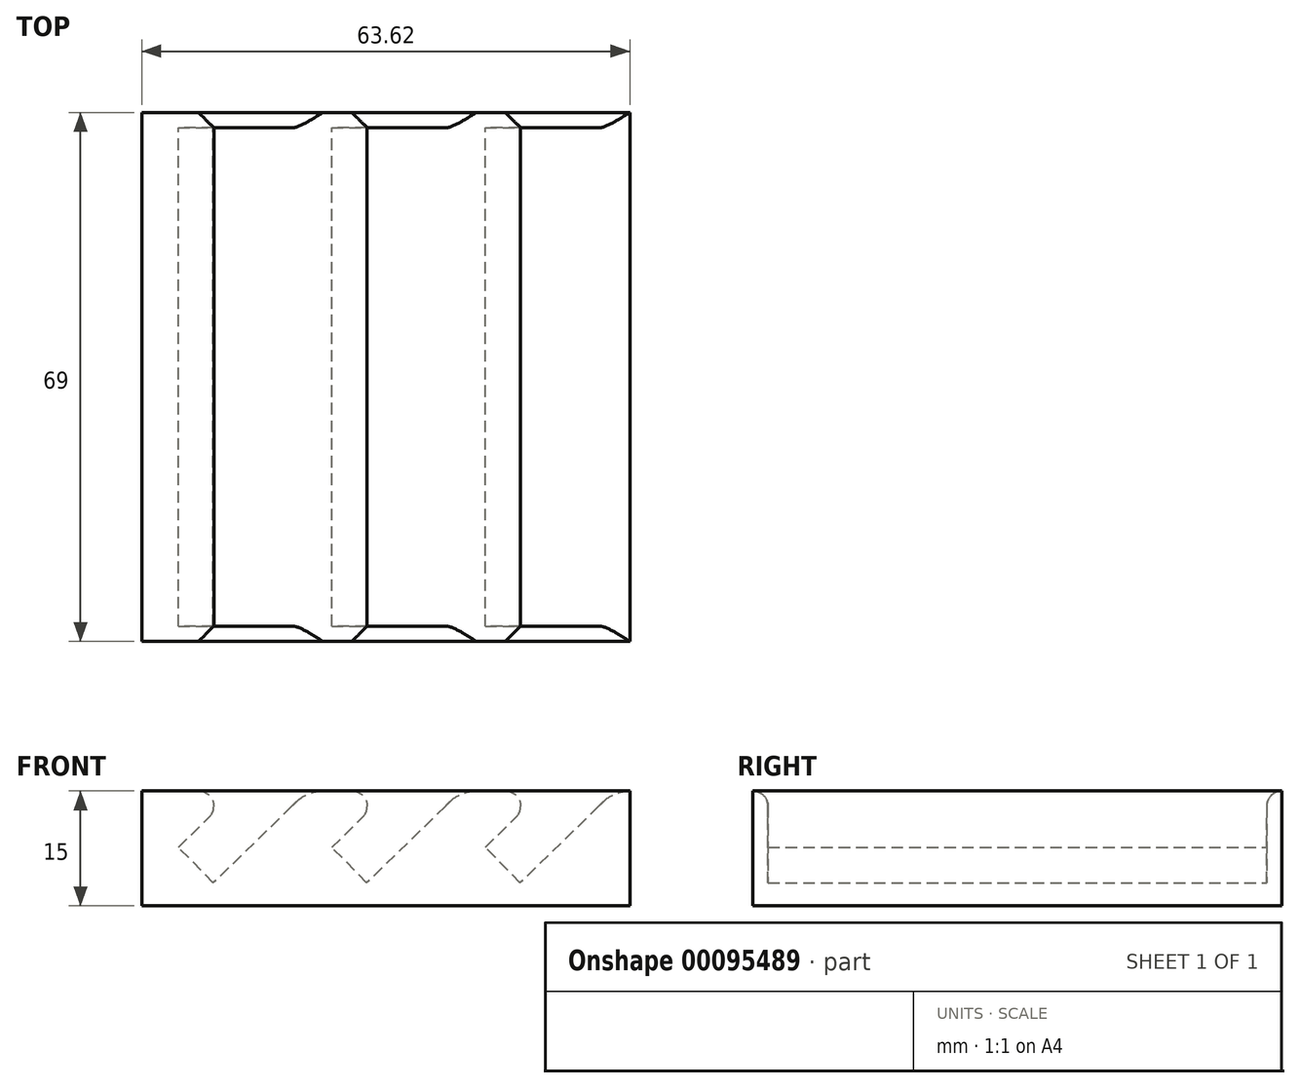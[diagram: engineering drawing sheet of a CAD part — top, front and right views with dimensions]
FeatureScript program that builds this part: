
annotation { "Feature Type Name" : "Feature", "Feature Type Description" : "" }
export const myFeature = defineFeature(function(context is Context, id is Id, definition is map)
    precondition{}
    {
        {
            var Q0;
            Q0=qCreatedBy(makeId("Front.planeOp"),FACE);
            var sketch = newSketch(context, id + "F0", { "sketchPlane" : qUnion([Q0])});
            skLineSegment(sketch, "E0.bottom", {"start": v(0, 0) * mm, "end": v(85.92, 0) * mm});
            skLineSegment(sketch, "E0.top", {"start": v(68.62, 15) * mm, "end": v(85.92, 15) * mm});
            skLineSegment(sketch, "E0.left", {"start": v(0, 0) * mm, "end": v(0, 15) * mm});
            skLineSegment(sketch, "E0.right", {"start": v(85.92, 0) * mm, "end": v(85.92, 15) * mm});
            skLineSegment(sketch, "E1", {"start": v(0, 3) * mm, "end": v(5, 3) * mm});
            skLineSegment(sketch, "E2", {"start": v(5, 3) * mm, "end": v(71.51, 68) * mm, "construction": true});
            skLineSegment(sketch, "E3", {"start": v(5, 3) * mm, "end": v(17.28, 15) * mm});
            skLineSegment(sketch, "E4", {"start": v(5, 3) * mm, "end": v(5.22, 3) * mm});
            skLineSegment(sketch, "E5", {"start": v(5.22, 3) * mm, "end": v(85.92, 3) * mm});
            skLineSegment(sketch, "E6", {"start": v(71.51, 68) * mm, "end": v(76.06, 63.35) * mm, "construction": true});
            skLineSegment(sketch, "E7", {"start": v(76.06, 63.35) * mm, "end": v(14.3, 3) * mm, "construction": true});
            skLineSegment(sketch, "E8", {"start": v(25.12, 13.58) * mm, "end": v(14.3, 3) * mm});
            skLineSegment(sketch, "E9.1.0.0", {"start": v(25, 3) * mm, "end": v(37.28, 15) * mm});
            skLineSegment(sketch, "E9.1.0.3", {"start": v(96.06, 63.35) * mm, "end": v(34.3, 3) * mm, "construction": true});
            skLineSegment(sketch, "E9.1.0.4", {"start": v(25, 3) * mm, "end": v(91.51, 68) * mm, "construction": true});
            skLineSegment(sketch, "E9.1.0.5", {"start": v(91.51, 68) * mm, "end": v(96.06, 63.35) * mm, "construction": true});
            skLineSegment(sketch, "E9.2.0.0", {"start": v(45, 3) * mm, "end": v(57.28, 15) * mm});
            skLineSegment(sketch, "E9.2.0.2", {"start": v(65.12, 13.58) * mm, "end": v(54.3, 3) * mm});
            skLineSegment(sketch, "E9.2.0.3", {"start": v(116.06, 63.35) * mm, "end": v(54.3, 3) * mm, "construction": true});
            skLineSegment(sketch, "E9.2.0.4", {"start": v(45, 3) * mm, "end": v(111.51, 68) * mm, "construction": true});
            skLineSegment(sketch, "E9.2.0.5", {"start": v(111.51, 68) * mm, "end": v(116.06, 63.35) * mm, "construction": true});
            skLineSegment(sketch, "E9.direction1", {"start": v(5, 3) * mm, "end": v(25, 3) * mm, "construction": true});
            skLineSegment(sketch, "E10", {"start": v(71.51, 68) * mm, "end": v(107.37, 31.3) * mm, "construction": true});
            skLineSegment(sketch, "E11", {"start": v(14.3, 3) * mm, "end": v(9.76, 7.65) * mm});
            skLineSegment(sketch, "E12", {"start": v(34.3, 3) * mm, "end": v(29.76, 7.65) * mm});
            skLineSegment(sketch, "E13", {"start": v(54.3, 3) * mm, "end": v(49.76, 7.65) * mm});
            skPoint(sketch, "E14.newPointA", {"position": v(32.44, 20.73) * mm});
            skArc(sketch, "E14.filletArc", {"start": v(28.62, 15) * mm, "mid": v(26.73, 14.63) * mm, "end": v(25.12, 13.58) * mm});
            skLineSegment(sketch, "E15", {"start": v(17.28, 15) * mm, "end": v(0, 15) * mm});
            skPoint(sketch, "E16.newPointA", {"position": v(72.44, 20.73) * mm});
            skArc(sketch, "E16.filletArc", {"start": v(68.62, 15) * mm, "mid": v(66.73, 14.63) * mm, "end": v(65.12, 13.58) * mm});
            skLineSegment(sketch, "E17", {"start": v(28.62, 15) * mm, "end": v(37.28, 15) * mm});
            skPoint(sketch, "E18.visualSharp", {"position": v(52.44, 20.73) * mm});
            skLineSegment(sketch, "E19", {"start": v(57.28, 15) * mm, "end": v(48.62, 15) * mm});
            skLineSegment(sketch, "E20", {"start": v(45.12, 13.58) * mm, "end": v(34.3, 3) * mm});
            skPoint(sketch, "E21.visualSharp", {"position": v(46.58, 15) * mm});
            skArc(sketch, "E21.filletArc", {"start": v(48.62, 15) * mm, "mid": v(46.73, 14.63) * mm, "end": v(45.12, 13.58) * mm});
            skLineSegment(sketch, "E22", {"start": v(5, 0) * mm, "end": v(5, 15) * mm});
            skLineSegment(sketch, "E23", {"start": v(68.62, 15) * mm, "end": v(68.62, 0) * mm});
            skSolve(sketch);
        }
        {
            var Q0;
            {var subQ1=sQuery(id+"F0.wireOp",EDGE,"E3");var subQ4=sQuery(id+"F0.wireOp",EDGE,"E15");var subQ5=makeQuery(id+"F0.imprint","INTERSECT",VERTEX,{"derivedFrom":[subQ1,subQ4]});Q0=makeQuery(id+"F0.imprint","IMPRINT",FACE,{"disambiguationData":[TD([[makeQuery(id+"F0.imprint","IMPRINT",EDGE,{"disambiguationData":[TD([[subQ5,1.0]])],"derivedFrom":subQ1}),1.0]])]});}
            var Q1;
            {var subQ0=sQuery(id+"F0.wireOp",EDGE,"E4");Q1=makeQuery(id+"F0.imprint","IMPRINT",FACE,{"disambiguationData":[TD([[makeQuery(id+"F0.imprint","IMPRINT",EDGE,{"derivedFrom":subQ0}),1.0]])]});}
            var Q2;
            {var subQ6=sQuery(id+"F0.wireOp",EDGE,"E4");Q2=makeQuery(id+"F0.imprint","IMPRINT",FACE,{"disambiguationData":[TD([[makeQuery(id+"F0.imprint","IMPRINT",EDGE,{"derivedFrom":subQ6}),-1.0]])]});}
            var Q3;
            {var subQ5=sQuery(id+"F0.wireOp",EDGE,"E8");Q3=makeQuery(id+"F0.imprint","IMPRINT",FACE,{"disambiguationData":[TD([[makeQuery(id+"F0.imprint","IMPRINT",EDGE,{"derivedFrom":subQ5}),1.0]])]});}
            var Q4;
            {var subQ3=sQuery(id+"F0.wireOp",EDGE,"E12");Q4=makeQuery(id+"F0.imprint","IMPRINT",FACE,{"disambiguationData":[TD([[makeQuery(id+"F0.imprint","IMPRINT",EDGE,{"derivedFrom":subQ3}),1.0]])]});}
            var Q5;
            {var subQ0=sQuery(id+"F0.wireOp",EDGE,"E19");Q5=makeQuery(id+"F0.imprint","IMPRINT",FACE,{"disambiguationData":[TD([[makeQuery(id+"F0.imprint","IMPRINT",EDGE,{"derivedFrom":subQ0}),1.0]])]});}
            var Q6;
            {var subQ3=sQuery(id+"F0.wireOp",EDGE,"E13");Q6=makeQuery(id+"F0.imprint","IMPRINT",FACE,{"disambiguationData":[TD([[makeQuery(id+"F0.imprint","IMPRINT",EDGE,{"derivedFrom":subQ3}),1.0]])]});}
            var Q7;
            {var subQ0=sQuery(id+"F0.wireOp",EDGE,"E9.2.0.2");Q7=makeQuery(id+"F0.imprint","IMPRINT",FACE,{"disambiguationData":[TD([[makeQuery(id+"F0.imprint","IMPRINT",EDGE,{"derivedFrom":subQ0}),1.0]])]});}
            extrude(context, id + "F1", {"entities" : qUnion([Q0, Q1, Q2, Q3, Q4, Q5, Q6, Q7]), "depth" : 65 * mm});
        }
        {
            var Q0;
            Q0=makeQuery(id+"F1.opExtrude","CAP_FACE",FACE,{"disambiguationData":[OSD([sQuery(id+"F0.wireOp",EDGE,"E0.bottom"),sQuery(id+"F0.wireOp",EDGE,"E3"),sQuery(id+"F0.wireOp",EDGE,"E8"),sQuery(id+"F0.wireOp",EDGE,"E9.1.0.0"),sQuery(id+"F0.wireOp",EDGE,"E9.2.0.0"),sQuery(id+"F0.wireOp",EDGE,"E9.2.0.2"),sQuery(id+"F0.wireOp",EDGE,"E11"),sQuery(id+"F0.wireOp",EDGE,"E12"),sQuery(id+"F0.wireOp",EDGE,"E13"),sQuery(id+"F0.wireOp",EDGE,"E14.filletArc"),sQuery(id+"F0.wireOp",EDGE,"E15"),sQuery(id+"F0.wireOp",EDGE,"E16.filletArc"),sQuery(id+"F0.wireOp",EDGE,"E17"),sQuery(id+"F0.wireOp",EDGE,"E19"),sQuery(id+"F0.wireOp",EDGE,"E20"),sQuery(id+"F0.wireOp",EDGE,"E21.filletArc"),sQuery(id+"F0.wireOp",EDGE,"E22"),sQuery(id+"F0.wireOp",EDGE,"E23")])],"isStart":false});
            var sketch = newSketch(context, id + "F2", { "sketchPlane" : qUnion([Q0])});
            skLineSegment(sketch, "E24.bottom", {"start": v(5, 15) * mm, "end": v(68.62, 15) * mm});
            skLineSegment(sketch, "E24.top", {"start": v(5, 0) * mm, "end": v(68.62, 0) * mm});
            skLineSegment(sketch, "E24.left", {"start": v(5, 15) * mm, "end": v(5, 0) * mm});
            skLineSegment(sketch, "E24.right", {"start": v(68.62, 15) * mm, "end": v(68.62, 0) * mm});
            skSolve(sketch);
        }
        {
            var Q0;
            Q0=makeQuery(id+"F2.imprint","IMPRINT",FACE,{"disambiguationData":[TD([[makeQuery(id+"F2.imprint","IMPRINT",EDGE,{"derivedFrom":sQuery(id+"F2.wireOp",EDGE,"E24.top")}),1.0]])]});
            var Q1;
            {var subQ0=makeQuery(id+"F1.opExtrude","CAP_EDGE",EDGE,{"disambiguationData":[OSD([sQuery(id+"F0.wireOp",EDGE,"E3")])],"isStart":false});Q1=makeQuery(id+"F2.imprint","IMPRINT",FACE,{"disambiguationData":[TD([[makeQuery(id+"F2.imprint","IMPRINT",EDGE,{"derivedFrom":subQ0}),-1.0]])]});}
            var Q2;
            {var subQ0=makeQuery(id+"F1.opExtrude","CAP_EDGE",EDGE,{"disambiguationData":[OSD([sQuery(id+"F0.wireOp",EDGE,"E9.1.0.0")])],"isStart":false});Q2=makeQuery(id+"F2.imprint","IMPRINT",FACE,{"disambiguationData":[TD([[makeQuery(id+"F2.imprint","IMPRINT",EDGE,{"derivedFrom":subQ0}),-1.0]])]});}
            var Q3;
            {var subQ1=makeQuery(id+"F1.opExtrude","CAP_EDGE",EDGE,{"disambiguationData":[OSD([sQuery(id+"F0.wireOp",EDGE,"E9.2.0.0")])],"isStart":false});Q3=makeQuery(id+"F2.imprint","IMPRINT",FACE,{"disambiguationData":[TD([[makeQuery(id+"F2.imprint","IMPRINT",EDGE,{"derivedFrom":subQ1}),-1.0]])]});}
            extrude(context, id + "F3", {"entities" : qUnion([Q0, Q1, Q2, Q3]), "operationType" : NewBodyOperationType.ADD, "depth" : 2 * mm});
        }
        {
            var Q0;
            Q0=makeQuery(id+"F1.opExtrude","CAP_FACE",FACE,{"disambiguationData":[OSD([sQuery(id+"F0.wireOp",EDGE,"E0.bottom"),sQuery(id+"F0.wireOp",EDGE,"E3"),sQuery(id+"F0.wireOp",EDGE,"E8"),sQuery(id+"F0.wireOp",EDGE,"E9.1.0.0"),sQuery(id+"F0.wireOp",EDGE,"E9.2.0.0"),sQuery(id+"F0.wireOp",EDGE,"E9.2.0.2"),sQuery(id+"F0.wireOp",EDGE,"E11"),sQuery(id+"F0.wireOp",EDGE,"E12"),sQuery(id+"F0.wireOp",EDGE,"E13"),sQuery(id+"F0.wireOp",EDGE,"E14.filletArc"),sQuery(id+"F0.wireOp",EDGE,"E15"),sQuery(id+"F0.wireOp",EDGE,"E16.filletArc"),sQuery(id+"F0.wireOp",EDGE,"E17"),sQuery(id+"F0.wireOp",EDGE,"E19"),sQuery(id+"F0.wireOp",EDGE,"E20"),sQuery(id+"F0.wireOp",EDGE,"E21.filletArc"),sQuery(id+"F0.wireOp",EDGE,"E22"),sQuery(id+"F0.wireOp",EDGE,"E23")])],"isStart":true});
            var sketch = newSketch(context, id + "F4", { "sketchPlane" : qUnion([Q0])});
            skLineSegment(sketch, "E25.bottom", {"start": v(-68.62, 15) * mm, "end": v(-5, 15) * mm});
            skLineSegment(sketch, "E25.top", {"start": v(-68.62, 0) * mm, "end": v(-5, 0) * mm});
            skLineSegment(sketch, "E25.left", {"start": v(-68.62, 15) * mm, "end": v(-68.62, 0) * mm});
            skLineSegment(sketch, "E25.right", {"start": v(-5, 15) * mm, "end": v(-5, 0) * mm});
            skSolve(sketch);
        }
        {
            var Q0;
            Q0=makeQuery(id+"F4.imprint","IMPRINT",FACE,{"disambiguationData":[TD([[makeQuery(id+"F4.imprint","IMPRINT",EDGE,{"derivedFrom":sQuery(id+"F4.wireOp",EDGE,"E25.top")}),-1.0]])]});
            var Q1;
            {var subQ1=makeQuery(id+"F1.opExtrude","CAP_EDGE",EDGE,{"disambiguationData":[OSD([sQuery(id+"F0.wireOp",EDGE,"E9.2.0.0")])],"isStart":true});Q1=makeQuery(id+"F4.imprint","IMPRINT",FACE,{"disambiguationData":[TD([[makeQuery(id+"F4.imprint","IMPRINT",EDGE,{"derivedFrom":subQ1}),1.0]])]});}
            var Q2;
            {var subQ0=makeQuery(id+"F1.opExtrude","CAP_EDGE",EDGE,{"disambiguationData":[OSD([sQuery(id+"F0.wireOp",EDGE,"E9.1.0.0")])],"isStart":true});Q2=makeQuery(id+"F4.imprint","IMPRINT",FACE,{"disambiguationData":[TD([[makeQuery(id+"F4.imprint","IMPRINT",EDGE,{"derivedFrom":subQ0}),1.0]])]});}
            var Q3;
            {var subQ1=makeQuery(id+"F1.opExtrude","CAP_EDGE",EDGE,{"disambiguationData":[OSD([sQuery(id+"F0.wireOp",EDGE,"E3")])],"isStart":true});Q3=makeQuery(id+"F4.imprint","IMPRINT",FACE,{"disambiguationData":[TD([[makeQuery(id+"F4.imprint","IMPRINT",EDGE,{"derivedFrom":subQ1}),1.0]])]});}
            extrude(context, id + "F5", {"entities" : qUnion([Q0, Q1, Q2, Q3]), "operationType" : NewBodyOperationType.ADD, "depth" : 2 * mm});
        }
        {
            var Q0;
            {var subQ0=sQuery(id+"F2.wireOp",EDGE,"E24.bottom");Q0=makeQuery(id+"F3.boolean.opBoolean","SPLIT",EDGE,{"disambiguationData":[TD([makeQuery(id+"F1.opExtrude","SWEPT_FACE",FACE,{"disambiguationData":[OSD([sQuery(id+"F0.wireOp",EDGE,"E9.2.0.0")])]})])],"derivedFrom":makeQuery(id+"F3.opExtrude","CAP_EDGE",EDGE,{"disambiguationData":[OSD([subQ0])],"isStart":true})});}
            var Q1;
            Q1=makeQuery(id+"F1.opExtrude","SWEPT_EDGE",EDGE,{"disambiguationData":[OSD([sQuery(id+"F0.wireOp",EDGE,"E9.2.0.0"),sQuery(id+"F0.wireOp",EDGE,"E19")])]});
            var Q2;
            {var subQ1=sQuery(id+"F4.wireOp",EDGE,"E25.bottom");Q2=makeQuery(id+"F5.boolean.opBoolean","SPLIT",EDGE,{"disambiguationData":[TD([makeQuery(id+"F1.opExtrude","SWEPT_FACE",FACE,{"disambiguationData":[OSD([sQuery(id+"F0.wireOp",EDGE,"E9.2.0.0")])]})])],"derivedFrom":makeQuery(id+"F5.opExtrude","CAP_EDGE",EDGE,{"disambiguationData":[OSD([subQ1])],"isStart":true})});}
            var Q3;
            {var subQ0=sQuery(id+"F4.wireOp",EDGE,"E25.bottom");Q3=makeQuery(id+"F5.boolean.opBoolean","SPLIT",EDGE,{"disambiguationData":[TD([makeQuery(id+"F1.opExtrude","SWEPT_FACE",FACE,{"disambiguationData":[OSD([sQuery(id+"F0.wireOp",EDGE,"E9.1.0.0")])]})])],"derivedFrom":makeQuery(id+"F5.opExtrude","CAP_EDGE",EDGE,{"disambiguationData":[OSD([subQ0])],"isStart":true})});}
            var Q4;
            Q4=makeQuery(id+"F1.opExtrude","SWEPT_EDGE",EDGE,{"disambiguationData":[OSD([sQuery(id+"F0.wireOp",EDGE,"E9.1.0.0"),sQuery(id+"F0.wireOp",EDGE,"E17")])]});
            var Q5;
            {var subQ0=sQuery(id+"F2.wireOp",EDGE,"E24.bottom");Q5=makeQuery(id+"F3.boolean.opBoolean","SPLIT",EDGE,{"disambiguationData":[TD([makeQuery(id+"F1.opExtrude","SWEPT_FACE",FACE,{"disambiguationData":[OSD([sQuery(id+"F0.wireOp",EDGE,"E9.1.0.0")])]})])],"derivedFrom":makeQuery(id+"F3.opExtrude","CAP_EDGE",EDGE,{"disambiguationData":[OSD([subQ0])],"isStart":true})});}
            var Q6;
            {var subQ0=sQuery(id+"F4.wireOp",EDGE,"E25.bottom");Q6=makeQuery(id+"F5.boolean.opBoolean","SPLIT",EDGE,{"disambiguationData":[TD([makeQuery(id+"F1.opExtrude","SWEPT_FACE",FACE,{"disambiguationData":[OSD([sQuery(id+"F0.wireOp",EDGE,"E3")])]})])],"derivedFrom":makeQuery(id+"F5.opExtrude","CAP_EDGE",EDGE,{"disambiguationData":[OSD([subQ0])],"isStart":true})});}
            var Q7;
            Q7=makeQuery(id+"F1.opExtrude","SWEPT_EDGE",EDGE,{"disambiguationData":[OSD([sQuery(id+"F0.wireOp",EDGE,"E3"),sQuery(id+"F0.wireOp",EDGE,"E15")])]});
            var Q8;
            {var subQ0=sQuery(id+"F2.wireOp",EDGE,"E24.bottom");Q8=makeQuery(id+"F3.boolean.opBoolean","SPLIT",EDGE,{"disambiguationData":[TD([makeQuery(id+"F1.opExtrude","SWEPT_FACE",FACE,{"disambiguationData":[OSD([sQuery(id+"F0.wireOp",EDGE,"E3")])]})])],"derivedFrom":makeQuery(id+"F3.opExtrude","CAP_EDGE",EDGE,{"disambiguationData":[OSD([subQ0])],"isStart":true})});}
            fillet(context, id + "F6", {"entities" : qUnion([Q0, Q1, Q2, Q3, Q4, Q5, Q6, Q7, Q8]), "radius" : 2 * mm, "tangentPropagation" : true, "allowEdgeOverflow" : false});
        }
    });
